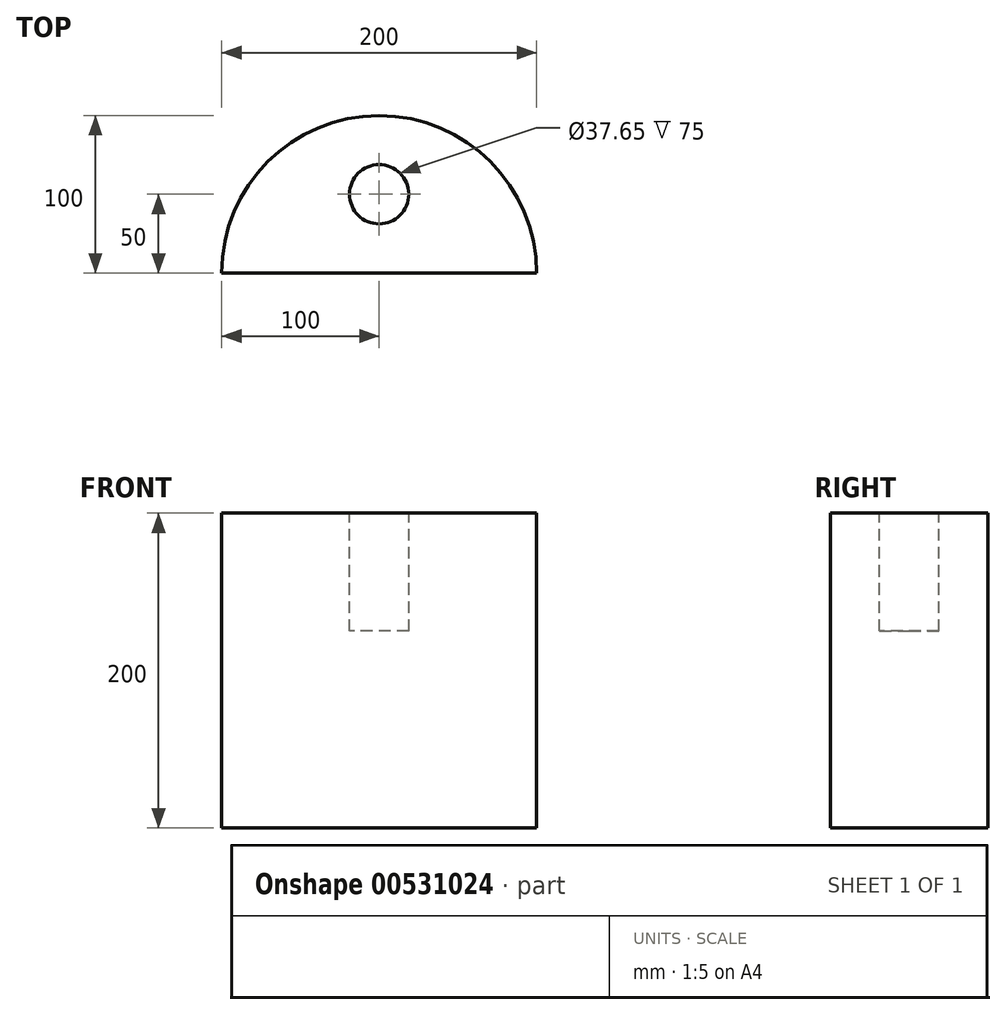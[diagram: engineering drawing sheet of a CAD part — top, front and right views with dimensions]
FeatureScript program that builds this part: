
annotation { "Feature Type Name" : "Feature", "Feature Type Description" : "" }
export const myFeature = defineFeature(function(context is Context, id is Id, definition is map)
    precondition{}
    {
        {
            var Q0;
            Q0=qCreatedBy(makeId("Top.planeOp"),FACE);
            var sketch = newSketch(context, id + "F0", { "sketchPlane" : qUnion([Q0])});
            skArc(sketch, "E0", {"start": v(100, 0) * mm, "mid": v(0, 100) * mm, "end": v(-100, 0) * mm});
            skLineSegment(sketch, "E1", {"start": v(-100, 0) * mm, "end": v(100, 0) * mm});
            skSolve(sketch);
        }
        {
            var Q0;
            Q0 = qSketchRegion(id + "F0", true);
            extrude(context, id + "F1", {"entities" : qUnion([Q0]), "endBound" : BoundingType.SYMMETRIC, "depth" : 200 * mm, "offsetDistance" : 25 * mm});
        }
        {
            var Q0;
            Q0=makeQuery(id+"F1.opExtrude","CAP_FACE",FACE,{"disambiguationData":[OSD([sQuery(id+"F0.wireOp",EDGE,"E0"),sQuery(id+"F0.wireOp",EDGE,"E1")])],"isStart":false});
            var sketch = newSketch(context, id + "F2", { "sketchPlane" : qUnion([Q0])});
            skCircle(sketch, "E2", {"center": v(0, 50) * mm, "radius": 18.83 * mm});
            skSolve(sketch);
        }
        {
            var Q0;
            Q0=makeQuery(id+"F2.imprint","IMPRINT",FACE,{"disambiguationData":[TD([[makeQuery(id+"F2.imprint","IMPRINT",EDGE,{"derivedFrom":sQuery(id+"F2.wireOp",EDGE,"E2")}),1.0]])]});
            extrude(context, id + "F3", {"entities" : qUnion([Q0]), "operationType" : NewBodyOperationType.REMOVE, "oppositeDirection" : true, "depth" : 75 * mm, "offsetDistance" : 25 * mm});
        }
    });
